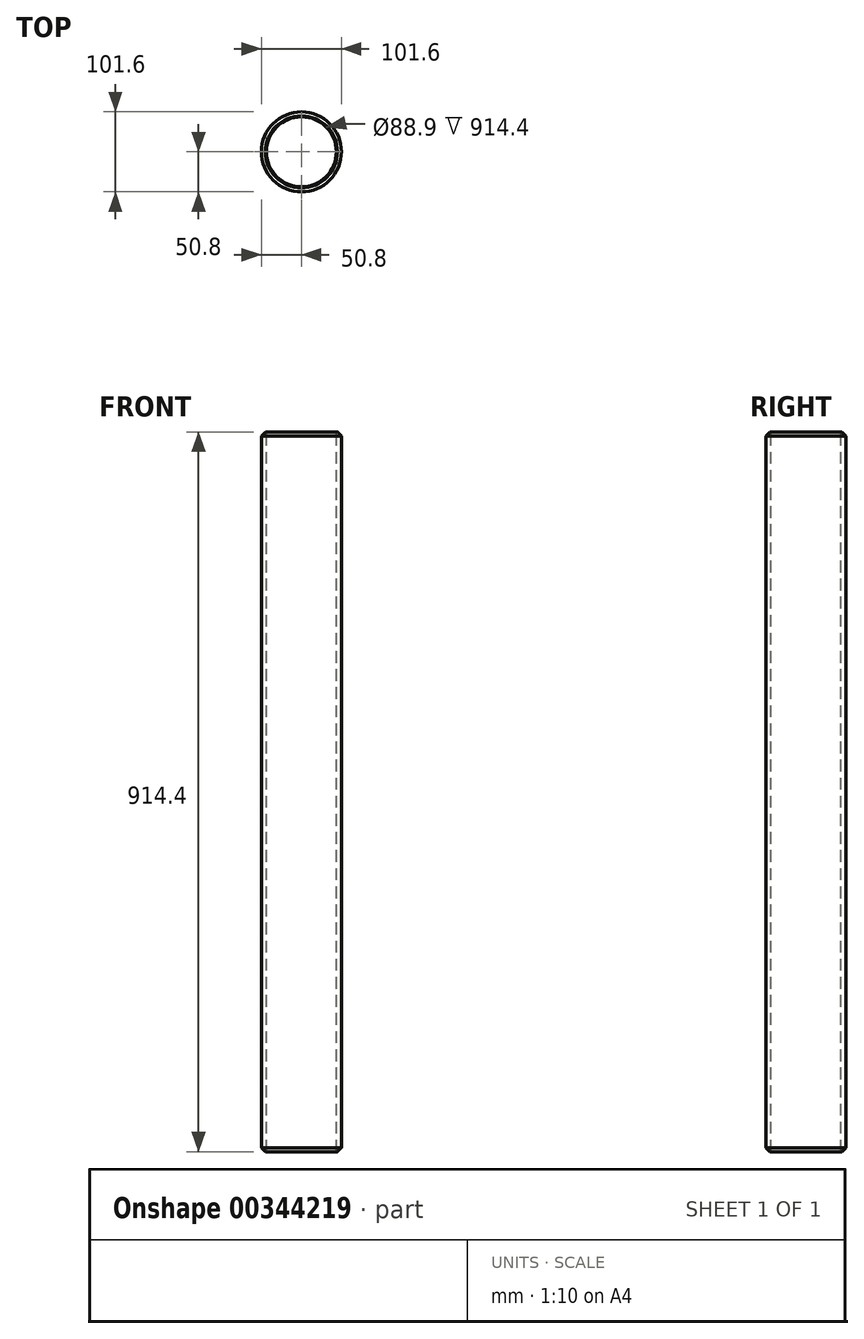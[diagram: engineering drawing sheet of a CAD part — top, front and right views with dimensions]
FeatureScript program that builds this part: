
annotation { "Feature Type Name" : "Feature", "Feature Type Description" : "" }
export const myFeature = defineFeature(function(context is Context, id is Id, definition is map)
    precondition{}
    {
        {
            var Q0;
            Q0=qCreatedBy(makeId("Top.planeOp"),FACE);
            var sketch = newSketch(context, id + "F0", { "sketchPlane" : qUnion([Q0])});
            skCircle(sketch, "E0", {"center": v(0, 0) * mm, "radius": 44.45 * mm});
            skCircle(sketch, "E1", {"center": v(0, 0) * mm, "radius": 50.8 * mm});
            skSolve(sketch);
        }
        {
            var Q0;
            Q0 = qSketchRegion(id + "F0", true);
            extrude(context, id + "F1", {"entities" : qUnion([Q0]), "oppositeDirection" : true, "depth" : 914.4 * mm});
        }
        {
            var Q0;
            Q0=makeQuery(id+"F1.opExtrude","CAP_EDGE",EDGE,{"disambiguationData":[OSD([sQuery(id+"F0.wireOp",EDGE,"E1")])],"isStart":true});
            chamfer(context, id + "F2", {"entities" : qUnion([Q0]), "width" : 5.08 * mm, "tangentPropagation" : true});
        }
        {
            var Q0;
            Q0=makeQuery(id+"F1.opExtrude","CAP_EDGE",EDGE,{"disambiguationData":[OSD([sQuery(id+"F0.wireOp",EDGE,"E1")])],"isStart":false});
            chamfer(context, id + "F3", {"entities" : qUnion([Q0]), "width" : 5.08 * mm, "tangentPropagation" : true});
        }
    });
